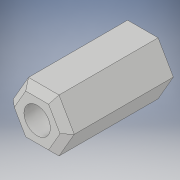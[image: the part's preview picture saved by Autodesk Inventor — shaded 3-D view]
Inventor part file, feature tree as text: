
AUTODESK INVENTOR PART (.ipt)
format: ipt  version: 2018 (Build 220112000, 112)  size: 106,496 bytes
history: native  units: in
note: dims shown in document units (in); Inventor stores cm internally (conversion verified against a paired STEP export)
features: extrude x1, chamfer x1, sketch x1
ambient origin geometry x8: Origin, YZ Plane, XZ Plane, XY Plane, X Axis, Y Axis, Z Axis, Center Point
bodies: Solid1 (feature_tree)
feature tree (3):
  extrude  "Extrusion1"  Depth=0.125in
  chamfer  "Chamfer1"  Distance=1.0in
  sketch  "Sketch1"  dims[d0=0.5in d1=0.25in d2=1.0in d3=0.0in d4=0.0625in d5=0.125in d6=45.0deg]
